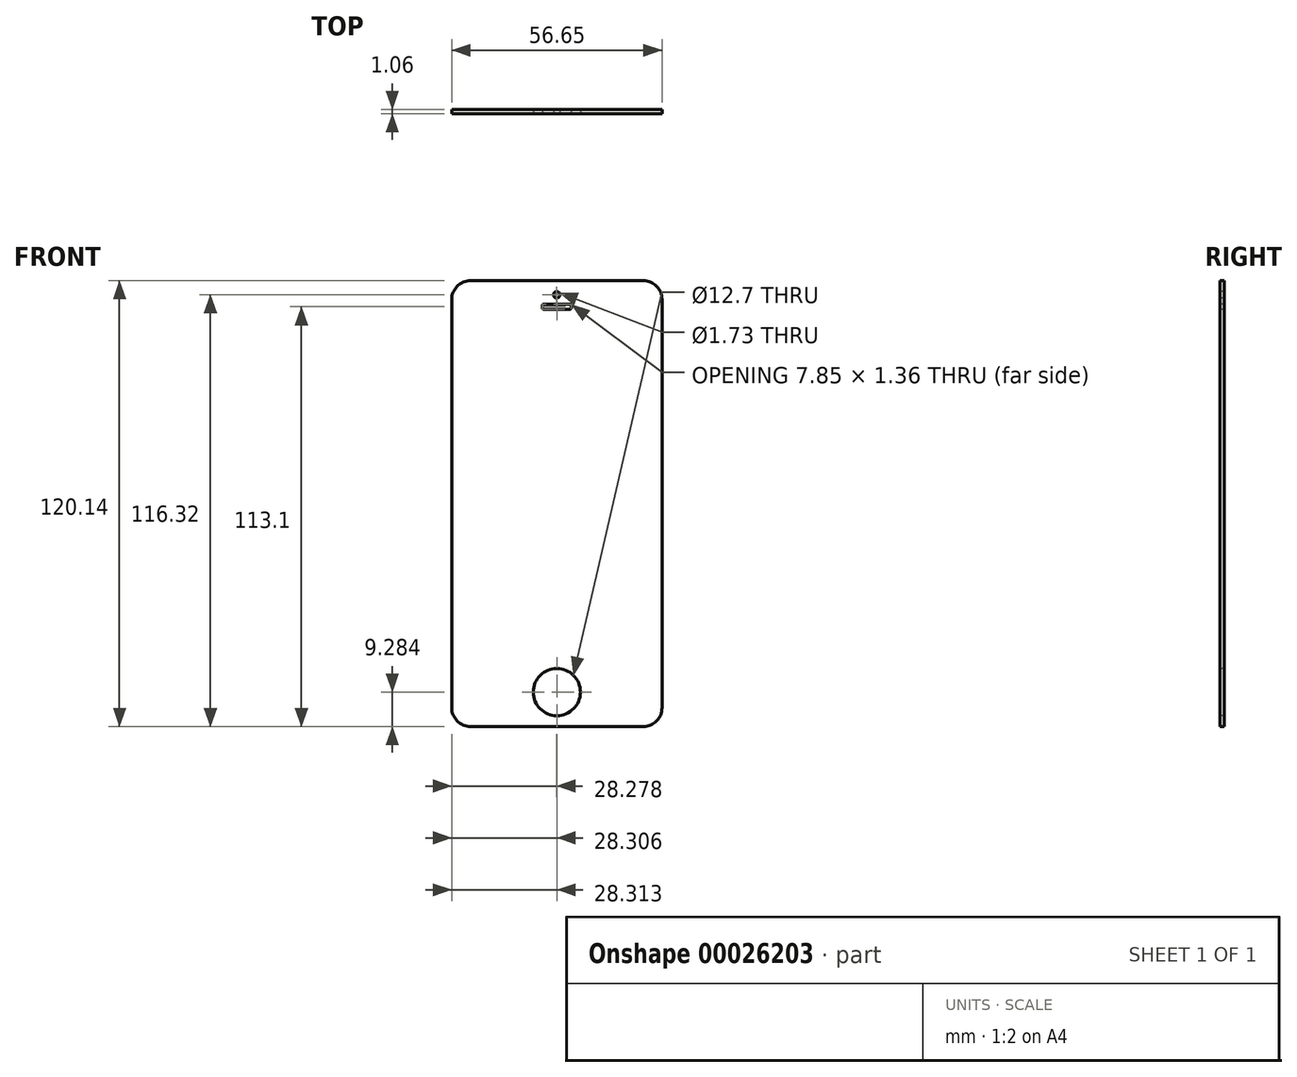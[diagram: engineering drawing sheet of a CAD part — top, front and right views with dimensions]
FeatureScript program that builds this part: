
annotation { "Feature Type Name" : "Feature", "Feature Type Description" : "" }
export const myFeature = defineFeature(function(context is Context, id is Id, definition is map)
    precondition{}
    {
        {
            var Q0;
            Q0=qCreatedBy(makeId("Front.planeOp"),FACE);
            var sketch = newSketch(context, id + "F0", { "sketchPlane" : qUnion([Q0])});
            skLineSegment(sketch, "E0.bottom", {"start": v(-52.49, 116) * mm, "end": v(4.16, 116) * mm});
            skLineSegment(sketch, "E0.top", {"start": v(-52.49, -4.14) * mm, "end": v(4.16, -4.14) * mm});
            skLineSegment(sketch, "E0.left", {"start": v(-52.49, 116) * mm, "end": v(-52.49, -4.14) * mm});
            skLineSegment(sketch, "E0.right", {"start": v(4.16, 116) * mm, "end": v(4.16, -4.14) * mm});
            skSolve(sketch);
        }
        {
            var Q0;
            Q0 = qSketchRegion(id + "F0", true);
            extrude(context, id + "F1", {"entities" : qUnion([Q0]), "depth" : 1.06 * mm});
        }
        {
            var Q0;
            Q0=makeQuery(id+"F1.opExtrude","SWEPT_EDGE",EDGE,{"disambiguationData":[OSD([sQuery(id+"F0.wireOp",EDGE,"E0.bottom"),sQuery(id+"F0.wireOp",EDGE,"E0.left")])]});
            var Q1;
            Q1=makeQuery(id+"F1.opExtrude","SWEPT_EDGE",EDGE,{"disambiguationData":[OSD([sQuery(id+"F0.wireOp",EDGE,"E0.top"),sQuery(id+"F0.wireOp",EDGE,"E0.left")])]});
            var Q2;
            Q2=makeQuery(id+"F1.opExtrude","SWEPT_EDGE",EDGE,{"disambiguationData":[OSD([sQuery(id+"F0.wireOp",EDGE,"E0.top"),sQuery(id+"F0.wireOp",EDGE,"E0.right")])]});
            var Q3;
            Q3=makeQuery(id+"F1.opExtrude","SWEPT_EDGE",EDGE,{"disambiguationData":[OSD([sQuery(id+"F0.wireOp",EDGE,"E0.bottom"),sQuery(id+"F0.wireOp",EDGE,"E0.right")])]});
            fillet(context, id + "F2", {"entities" : qUnion([Q0, Q1, Q2, Q3]), "radius" : 5.08 * mm, "tangentPropagation" : true, "allowEdgeOverflow" : false});
        }
        {
            var Q0;
            Q0=makeQuery(id+"F1.opExtrude","CAP_FACE",FACE,{"disambiguationData":[OSD([sQuery(id+"F0.wireOp",EDGE,"E0.bottom"),sQuery(id+"F0.wireOp",EDGE,"E0.top"),sQuery(id+"F0.wireOp",EDGE,"E0.left"),sQuery(id+"F0.wireOp",EDGE,"E0.right")])],"isStart":false});
            var sketch = newSketch(context, id + "F3", { "sketchPlane" : qUnion([Q0])});
            skCircle(sketch, "E1", {"center": v(-24.18, 5.14) * mm, "radius": 6.35 * mm});
            skSolve(sketch);
        }
        {
            var Q0;
            Q0 = qSketchRegion(id + "F3", true);
            extrude(context, id + "F4", {"entities" : qUnion([Q0]), "operationType" : NewBodyOperationType.REMOVE, "oppositeDirection" : true, "depth" : 25.4 * mm});
        }
        {
            var Q0;
            Q0=makeQuery(id+"F1.opExtrude","CAP_FACE",FACE,{"disambiguationData":[OSD([sQuery(id+"F0.wireOp",EDGE,"E0.bottom"),sQuery(id+"F0.wireOp",EDGE,"E0.top"),sQuery(id+"F0.wireOp",EDGE,"E0.left"),sQuery(id+"F0.wireOp",EDGE,"E0.right")])],"isStart":false});
            var sketch = newSketch(context, id + "F5", { "sketchPlane" : qUnion([Q0])});
            skCircle(sketch, "E2", {"center": v(-24.21, 112.18) * mm, "radius": 0.86 * mm});
            skLineSegment(sketch, "E3.bottom", {"start": v(-27.7, 109.64) * mm, "end": v(-20.66, 109.64) * mm});
            skLineSegment(sketch, "E3.top", {"start": v(-27.7, 108.28) * mm, "end": v(-20.66, 108.28) * mm});
            skLineSegment(sketch, "E3.left", {"start": v(-28.11, 109.24) * mm, "end": v(-28.11, 108.68) * mm});
            skLineSegment(sketch, "E3.right", {"start": v(-20.26, 109.24) * mm, "end": v(-20.26, 108.68) * mm});
            skPoint(sketch, "E4.visualSharp", {"position": v(-28.11, 109.64) * mm});
            skArc(sketch, "E4.filletArc", {"start": v(-27.7, 109.64) * mm, "mid": v(-28, 109.52) * mm, "end": v(-28.11, 109.24) * mm});
            skPoint(sketch, "E5.visualSharp", {"position": v(-20.26, 109.64) * mm});
            skArc(sketch, "E5.filletArc", {"start": v(-20.26, 109.24) * mm, "mid": v(-20.37, 109.52) * mm, "end": v(-20.66, 109.64) * mm});
            skPoint(sketch, "E6.visualSharp", {"position": v(-28.11, 108.28) * mm});
            skArc(sketch, "E6.filletArc", {"start": v(-28.11, 108.68) * mm, "mid": v(-28, 108.4) * mm, "end": v(-27.7, 108.28) * mm});
            skPoint(sketch, "E7.visualSharp", {"position": v(-20.26, 108.28) * mm});
            skArc(sketch, "E7.filletArc", {"start": v(-20.66, 108.28) * mm, "mid": v(-20.37, 108.4) * mm, "end": v(-20.26, 108.68) * mm});
            skSolve(sketch);
        }
        {
            var Q0;
            Q0 = qSketchRegion(id + "F5", true);
            extrude(context, id + "F6", {"entities" : qUnion([Q0]), "operationType" : NewBodyOperationType.REMOVE, "oppositeDirection" : true, "depth" : 25.4 * mm});
        }
    });
